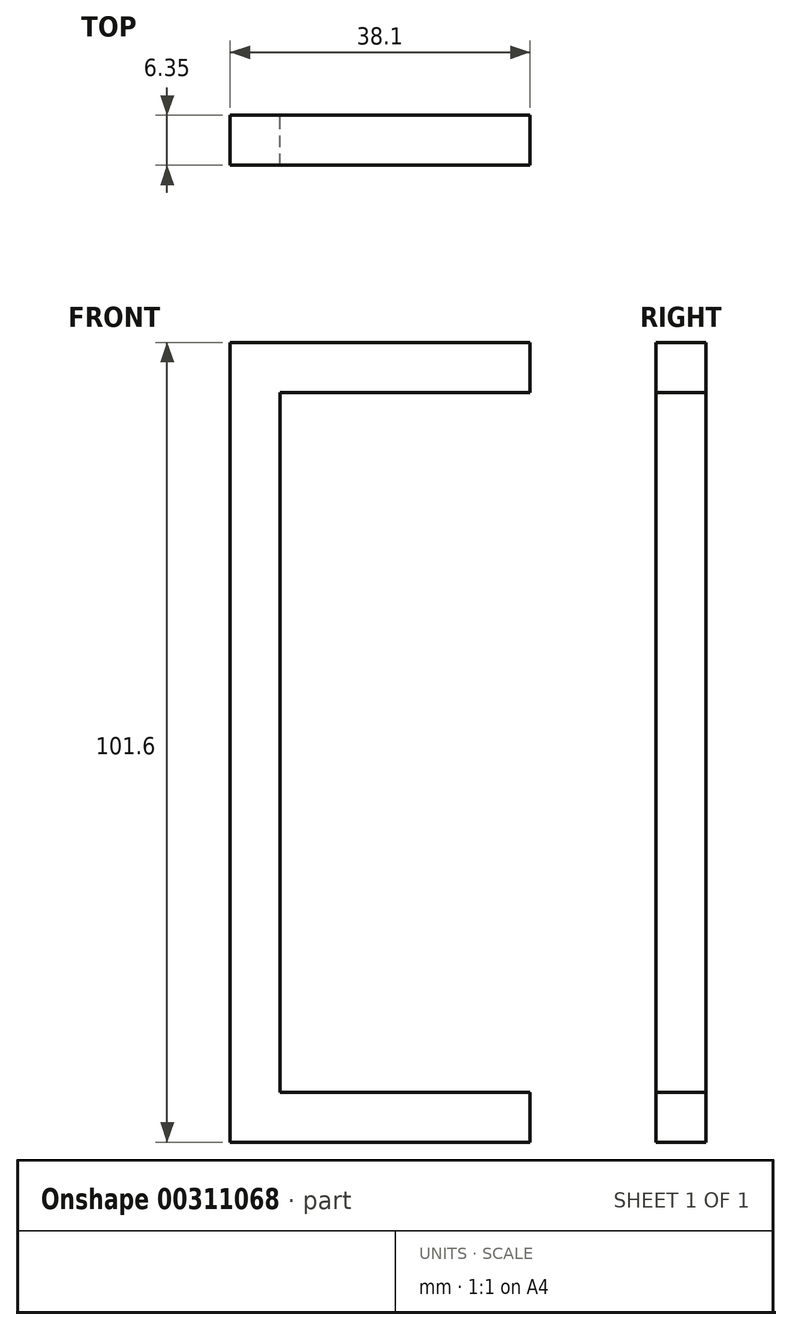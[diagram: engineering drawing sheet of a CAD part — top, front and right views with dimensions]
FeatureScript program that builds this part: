
annotation { "Feature Type Name" : "Feature", "Feature Type Description" : "" }
export const myFeature = defineFeature(function(context is Context, id is Id, definition is map)
    precondition{}
    {
        {
            var Q0;
            Q0=qCreatedBy(makeId("Front.planeOp"),FACE);
            var sketch = newSketch(context, id + "F0", { "sketchPlane" : qUnion([Q0])});
            skLineSegment(sketch, "E0", {"start": v(0, 0) * mm, "end": v(0, 101.6) * mm});
            skLineSegment(sketch, "E1", {"start": v(0, 101.6) * mm, "end": v(38.1, 101.6) * mm});
            skLineSegment(sketch, "E2", {"start": v(38.1, 101.6) * mm, "end": v(38.1, 95.25) * mm});
            skLineSegment(sketch, "E3", {"start": v(38.1, 95.25) * mm, "end": v(6.35, 95.25) * mm});
            skLineSegment(sketch, "E4", {"start": v(6.35, 95.25) * mm, "end": v(6.35, 6.35) * mm});
            skLineSegment(sketch, "E5", {"start": v(6.35, 6.35) * mm, "end": v(38.1, 6.35) * mm});
            skLineSegment(sketch, "E6", {"start": v(38.1, 6.35) * mm, "end": v(38.1, 0) * mm});
            skLineSegment(sketch, "E7", {"start": v(38.1, 0) * mm, "end": v(0, 0) * mm});
            skSolve(sketch);
        }
        {
            var Q0;
            Q0 = qSketchRegion(id + "F0", true);
            extrude(context, id + "F1", {"entities" : qUnion([Q0]), "depth" : 6.35 * mm});
        }
    });
